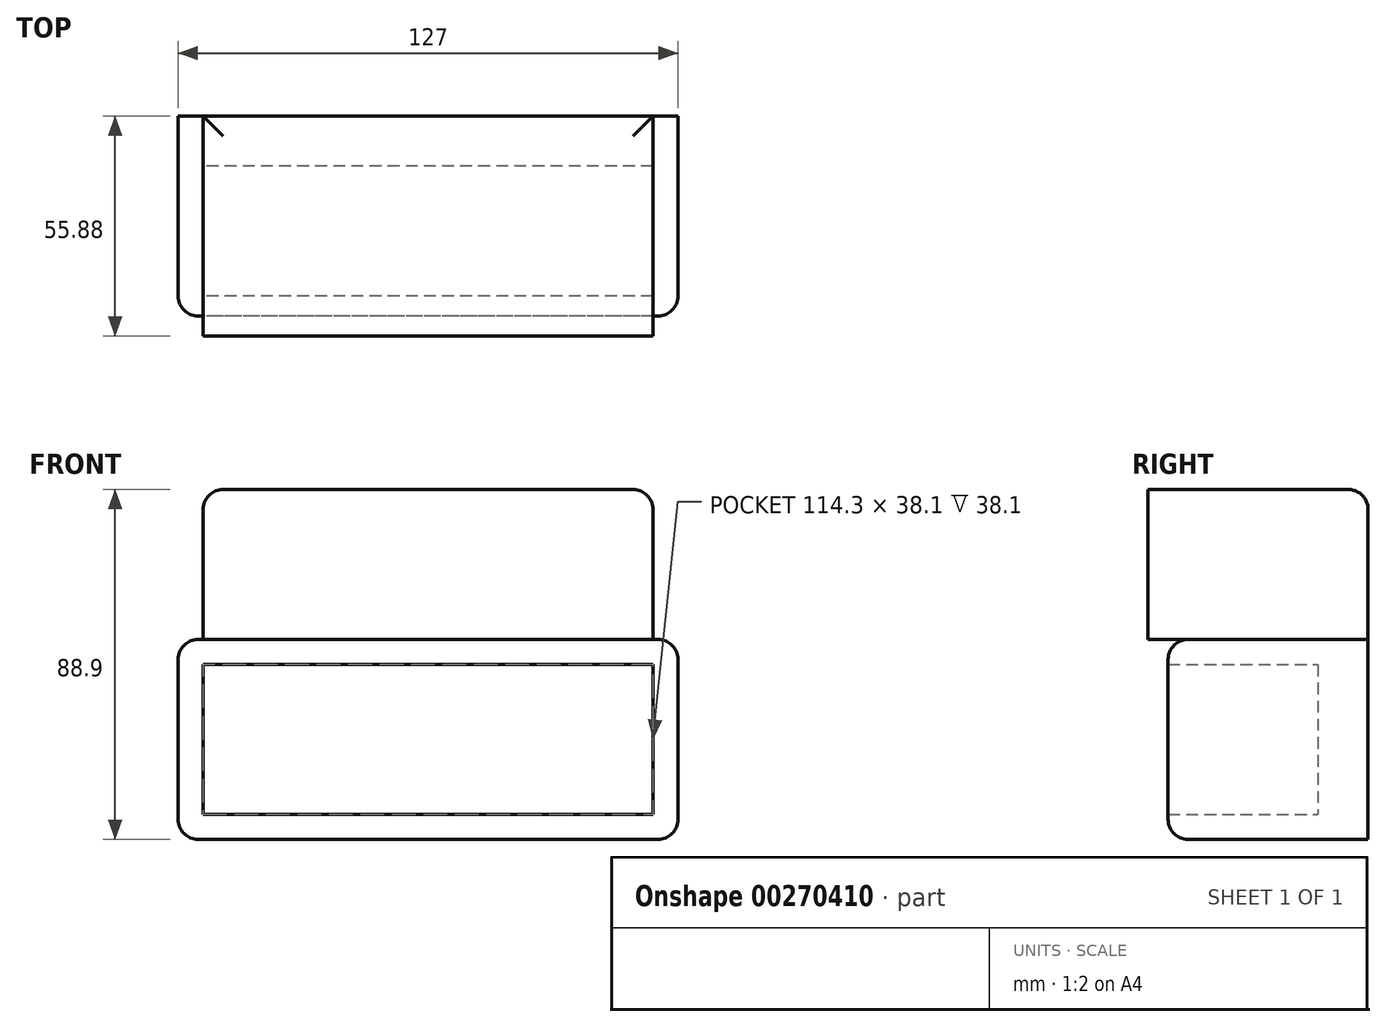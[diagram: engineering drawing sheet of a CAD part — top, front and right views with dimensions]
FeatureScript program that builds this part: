
annotation { "Feature Type Name" : "Feature", "Feature Type Description" : "" }
export const myFeature = defineFeature(function(context is Context, id is Id, definition is map)
    precondition{}
    {
        {
            var Q0;
            Q0=qCreatedBy(makeId("Front.planeOp"),FACE);
            var sketch = newSketch(context, id + "F0", { "sketchPlane" : qUnion([Q0])});
            skLineSegment(sketch, "E0.bottom", {"start": v(63.5, 25.4) * mm, "end": v(-63.5, 25.4) * mm});
            skLineSegment(sketch, "E0.top", {"start": v(63.5, -25.4) * mm, "end": v(-63.5, -25.4) * mm});
            skLineSegment(sketch, "E0.left", {"start": v(63.5, 25.4) * mm, "end": v(63.5, -25.4) * mm});
            skLineSegment(sketch, "E0.right", {"start": v(-63.5, 25.4) * mm, "end": v(-63.5, -25.4) * mm});
            skPoint(sketch, "E0.middle", {"position": v(0, 0) * mm});
            skLineSegment(sketch, "E1.bottom", {"start": v(57.15, 19.05) * mm, "end": v(-57.15, 19.05) * mm});
            skLineSegment(sketch, "E1.top", {"start": v(57.15, -19.05) * mm, "end": v(-57.15, -19.05) * mm});
            skLineSegment(sketch, "E1.left", {"start": v(57.15, 19.05) * mm, "end": v(57.15, -19.05) * mm});
            skLineSegment(sketch, "E1.right", {"start": v(-57.15, 19.05) * mm, "end": v(-57.15, -19.05) * mm});
            skLineSegment(sketch, "E2", {"start": v(0, 25.4) * mm, "end": v(0, 44.45) * mm});
            skLineSegment(sketch, "E3.bottom", {"start": v(57.15, 25.4) * mm, "end": v(-57.15, 25.4) * mm});
            skLineSegment(sketch, "E3.top", {"start": v(57.15, 63.5) * mm, "end": v(-57.15, 63.5) * mm});
            skLineSegment(sketch, "E3.left", {"start": v(57.15, 25.4) * mm, "end": v(57.15, 63.5) * mm});
            skLineSegment(sketch, "E3.right", {"start": v(-57.15, 25.4) * mm, "end": v(-57.15, 63.5) * mm});
            skPoint(sketch, "E3.middle", {"position": v(0, 44.45) * mm});
            skPoint(sketch, "E4", {"position": v(-28.58, 44.45) * mm});
            skPoint(sketch, "E5", {"position": v(28.58, 44.45) * mm});
            skLineSegment(sketch, "E6", {"start": v(0, 44.45) * mm, "end": v(-28.58, 44.45) * mm});
            skLineSegment(sketch, "E7", {"start": v(0, 44.45) * mm, "end": v(28.58, 44.45) * mm});
            skSolve(sketch);
        }
        {
            var Q0;
            Q0=makeQuery(id+"F0.imprint","IMPRINT",FACE,{"disambiguationData":[TD([[makeQuery(id+"F0.imprint","IMPRINT",EDGE,{"derivedFrom":sQuery(id+"F0.wireOp",EDGE,"E0.top")}),-1.0]])]});
            extrude(context, id + "F1", {"entities" : qUnion([Q0]), "depth" : 50.8 * mm});
        }
        {
            var Q0;
            Q0=makeQuery(id+"F0.imprint","IMPRINT",FACE,{"disambiguationData":[TD([[makeQuery(id+"F0.imprint","IMPRINT",EDGE,{"derivedFrom":sQuery(id+"F0.wireOp",EDGE,"E1.bottom")}),1.0]])]});
            extrude(context, id + "F2", {"entities" : qUnion([Q0]), "operationType" : NewBodyOperationType.ADD, "depth" : 12.7 * mm});
        }
        {
            var Q0;
            Q0=makeQuery(id+"F1.opExtrude","SWEPT_EDGE",EDGE,{"disambiguationData":[OSD([sQuery(id+"F0.wireOp",EDGE,"E0.bottom"),sQuery(id+"F0.wireOp",EDGE,"E0.right")])]});
            var Q1;
            Q1=makeQuery(id+"F1.opExtrude","SWEPT_EDGE",EDGE,{"disambiguationData":[OSD([sQuery(id+"F0.wireOp",EDGE,"E0.top"),sQuery(id+"F0.wireOp",EDGE,"E0.right")])]});
            var Q2;
            Q2=makeQuery(id+"F1.opExtrude","SWEPT_EDGE",EDGE,{"disambiguationData":[OSD([sQuery(id+"F0.wireOp",EDGE,"E0.top"),sQuery(id+"F0.wireOp",EDGE,"E0.left")])]});
            var Q3;
            Q3=makeQuery(id+"F1.opExtrude","SWEPT_EDGE",EDGE,{"disambiguationData":[OSD([sQuery(id+"F0.wireOp",EDGE,"E0.bottom"),sQuery(id+"F0.wireOp",EDGE,"E0.left")])]});
            var Q4;
            Q4=makeQuery(id+"F1.opExtrude","CAP_EDGE",EDGE,{"disambiguationData":[OSD([sQuery(id+"F0.wireOp",EDGE,"E0.bottom"),sQuery(id+"F0.wireOp",EDGE,"E3.bottom")])],"isStart":false});
            var Q5;
            Q5=makeQuery(id+"F1.opExtrude","CAP_EDGE",EDGE,{"disambiguationData":[OSD([sQuery(id+"F0.wireOp",EDGE,"E0.right")])],"isStart":false});
            var Q6;
            Q6=makeQuery(id+"F1.opExtrude","CAP_EDGE",EDGE,{"disambiguationData":[OSD([sQuery(id+"F0.wireOp",EDGE,"E0.top")])],"isStart":false});
            var Q7;
            Q7=makeQuery(id+"F1.opExtrude","CAP_EDGE",EDGE,{"disambiguationData":[OSD([sQuery(id+"F0.wireOp",EDGE,"E0.left")])],"isStart":false});
            fillet(context, id + "F3", {"entities" : qUnion([Q0, Q1, Q2, Q3, Q4, Q5, Q6, Q7]), "radius" : 5.08 * mm, "tangentPropagation" : true, "allowEdgeOverflow" : false});
        }
        {
            var Q0;
            Q0=makeQuery(id+"F0.imprint","IMPRINT",FACE,{"disambiguationData":[TD([[makeQuery(id+"F0.imprint","IMPRINT",EDGE,{"derivedFrom":sQuery(id+"F0.wireOp",EDGE,"E3.top")}),1.0]])]});
            extrude(context, id + "F4", {"entities" : qUnion([Q0]), "operationType" : NewBodyOperationType.ADD, "depth" : 55.88 * mm});
        }
        {
            var Q0;
            Q0=makeQuery(id+"F4.opExtrude","SWEPT_EDGE",EDGE,{"disambiguationData":[OSD([sQuery(id+"F0.wireOp",EDGE,"E3.top"),sQuery(id+"F0.wireOp",EDGE,"E3.right")])]});
            var Q1;
            Q1=makeQuery(id+"F4.opExtrude","SWEPT_EDGE",EDGE,{"disambiguationData":[OSD([sQuery(id+"F0.wireOp",EDGE,"E3.top"),sQuery(id+"F0.wireOp",EDGE,"E3.left")])]});
            var Q2;
            Q2=makeQuery(id+"F4.opExtrude","CAP_EDGE",EDGE,{"disambiguationData":[OSD([sQuery(id+"F0.wireOp",EDGE,"E3.top")])],"isStart":true});
            fillet(context, id + "F5", {"entities" : qUnion([Q0, Q1, Q2]), "radius" : 5.08 * mm, "tangentPropagation" : true, "allowEdgeOverflow" : false});
        }
    });
